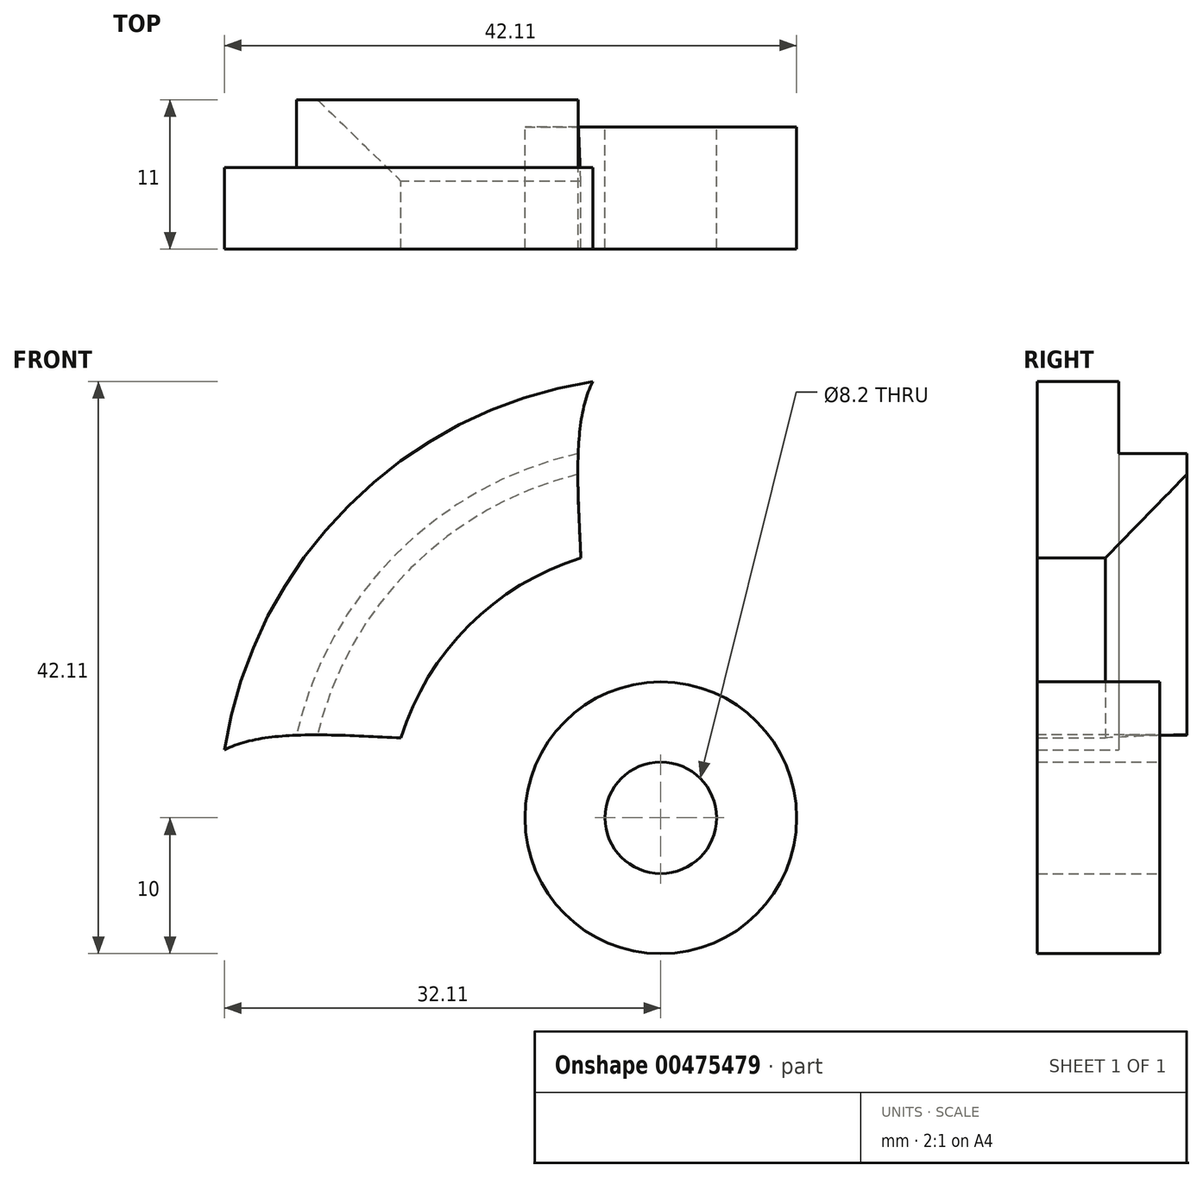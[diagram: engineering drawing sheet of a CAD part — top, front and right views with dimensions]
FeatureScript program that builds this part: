
annotation { "Feature Type Name" : "Feature", "Feature Type Description" : "" }
export const myFeature = defineFeature(function(context is Context, id is Id, definition is map)
    precondition{}
    {
        {
            var Q0;
            Q0=qCreatedBy(makeId("Front.planeOp"),FACE);
            var sketch = newSketch(context, id + "F0", { "sketchPlane" : qUnion([Q0])});
            skArc(sketch, "E0", {"start": v(-22.98, 22.98) * mm, "mid": v(-14.72, -28.98) * mm, "end": v(32.11, -5) * mm});
            skCircle(sketch, "E1", {"center": v(0, 0) * mm, "radius": 27.5 * mm});
            skLineSegment(sketch, "E2", {"start": v(-27.5, 0) * mm, "end": v(27.5, 0) * mm, "construction": true});
            skLineSegment(sketch, "E3", {"start": v(0, 0) * mm, "end": v(22.98, 22.98) * mm, "construction": true});
            skFitSpline(sketch, "E4", {"points": [v(5, 32.11) * mm, v(8, 8) * mm, v(32.11, 5) * mm], "startDerivative": vector(18, -34.81) * mm, "endDerivative": vector(34.81, -18) * mm});
            skArc(sketch, "E5.MirrorC", {"start": v(-5, 32.11) * mm, "mid": v(0, 32.5) * mm, "end": v(5, 32.11) * mm});
            skLineSegment(sketch, "E6.MirrorCS", {"start": v(0, 0) * mm, "end": v(-19.45, 19.45) * mm, "construction": true});
            skFitSpline(sketch, "E7.MirrorCS", {"points": [v(-5, 32.11) * mm, v(-8, 8) * mm, v(-32.11, 5) * mm], "startDerivative": vector(-18, -34.81) * mm, "endDerivative": vector(-34.81, -18) * mm});
            skFitSpline(sketch, "E8.MirrorCS", {"points": [v(-5, 32.11) * mm, v(-8, 8) * mm, v(-32.11, 5) * mm], "startDerivative": vector(-18, -34.81) * mm, "endDerivative": vector(-34.81, -18) * mm});
            skFitSpline(sketch, "E9.MirrorCS", {"points": [v(5, 32.11) * mm, v(8, 8) * mm, v(32.11, 5) * mm], "startDerivative": vector(18, -34.81) * mm, "endDerivative": vector(34.81, -18) * mm});
            skFitSpline(sketch, "E10.MirrorCS", {"points": [v(-5, 32.11) * mm, v(-8, 8) * mm, v(-32.11, 5) * mm], "startDerivative": vector(-18, -34.81) * mm, "endDerivative": vector(-34.81, -18) * mm});
            skFitSpline(sketch, "E11.MirrorCS", {"points": [v(5, 32.11) * mm, v(8, 8) * mm, v(32.11, 5) * mm], "startDerivative": vector(18, -34.81) * mm, "endDerivative": vector(34.81, -18) * mm});
            skLineSegment(sketch, "E12.MirrorCS", {"start": v(0, 0) * mm, "end": v(19.45, 19.45) * mm, "construction": true});
            skFitSpline(sketch, "E13.MirrorCS", {"points": [v(-5, 32.11) * mm, v(-8, 8) * mm, v(-32.11, 5) * mm], "startDerivative": vector(-18, -34.81) * mm, "endDerivative": vector(-34.81, -18) * mm});
            skFitSpline(sketch, "E14.MirrorCS", {"points": [v(5, 32.11) * mm, v(8, 8) * mm, v(32.11, 5) * mm], "startDerivative": vector(18, -34.81) * mm, "endDerivative": vector(34.81, -18) * mm});
            skLineSegment(sketch, "E15.MirrorCS", {"start": v(0, 0) * mm, "end": v(-8, 8) * mm, "construction": true});
            skArc(sketch, "E16.MirrorC", {"start": v(-32.11, 5) * mm, "mid": v(-5, -32.11) * mm, "end": v(32.11, -5) * mm});
            skFitSpline(sketch, "E17.MirrorCS", {"points": [v(-5, 32.11) * mm, v(-8, 8) * mm, v(-32.11, 5) * mm], "startDerivative": vector(-18, -34.81) * mm, "endDerivative": vector(-34.81, -18) * mm});
            skFitSpline(sketch, "E18.MirrorCS", {"points": [v(5, 32.11) * mm, v(8, 8) * mm, v(32.11, 5) * mm], "startDerivative": vector(18, -34.81) * mm, "endDerivative": vector(34.81, -18) * mm});
            skFitSpline(sketch, "E19.MirrorCS", {"points": [v(-5, 32.11) * mm, v(-8, 8) * mm, v(-32.11, 5) * mm], "startDerivative": vector(-18, -34.81) * mm, "endDerivative": vector(-34.81, -18) * mm});
            skArc(sketch, "E20.MirrorC", {"start": v(-6.08, 26.82) * mm, "mid": v(13.29, -24.08) * mm, "end": v(-19.45, 19.45) * mm});
            skFitSpline(sketch, "E21.MirrorCS", {"points": [v(5, 32.11) * mm, v(8, 8) * mm, v(32.11, 5) * mm], "startDerivative": vector(18, -34.81) * mm, "endDerivative": vector(34.81, -18) * mm});
            skCircle(sketch, "E22.MirrorC", {"center": v(0, 0) * mm, "radius": 32.5 * mm});
            skLineSegment(sketch, "E23.MirrorCS", {"start": v(0, 0) * mm, "end": v(-25.12, 25.12) * mm, "construction": true});
            skFitSpline(sketch, "E24.MirrorCS", {"points": [v(-5, 32.11) * mm, v(-8, 8) * mm, v(-32.11, 5) * mm], "startDerivative": vector(-18, -34.81) * mm, "endDerivative": vector(-34.81, -18) * mm});
            skLineSegment(sketch, "E25.MirrorCS", {"start": v(0, 0) * mm, "end": v(25.12, 25.12) * mm, "construction": true});
            skFitSpline(sketch, "E26.MirrorCS", {"points": [v(-5, 32.11) * mm, v(-8, 8) * mm, v(-32.11, 5) * mm], "startDerivative": vector(-18, -34.81) * mm, "endDerivative": vector(-34.81, -18) * mm});
            skFitSpline(sketch, "E27.MirrorCS", {"points": [v(5, 32.11) * mm, v(8, 8) * mm, v(32.11, 5) * mm], "startDerivative": vector(18, -34.81) * mm, "endDerivative": vector(34.81, -18) * mm});
            skLineSegment(sketch, "E28.MirrorCS", {"start": v(27.5, 0) * mm, "end": v(-27.5, 0) * mm, "construction": true});
            skFitSpline(sketch, "E29.MirrorCS", {"points": [v(-5, -32.11) * mm, v(-8, -8) * mm, v(-32.11, -5) * mm], "startDerivative": vector(-18, 34.81) * mm, "endDerivative": vector(-34.81, 18) * mm});
            skFitSpline(sketch, "E30.MirrorCS", {"points": [v(5, -32.11) * mm, v(8, -8) * mm, v(32.11, -5) * mm], "startDerivative": vector(18, 34.81) * mm, "endDerivative": vector(34.81, 18) * mm});
            skFitSpline(sketch, "E31.MirrorCS", {"points": [v(-5, -32.11) * mm, v(-8, -8) * mm, v(-32.11, -5) * mm], "startDerivative": vector(-18, 34.81) * mm, "endDerivative": vector(-34.81, 18) * mm});
            skFitSpline(sketch, "E32.MirrorCS", {"points": [v(5, -32.11) * mm, v(8, -8) * mm, v(32.11, -5) * mm], "startDerivative": vector(18, 34.81) * mm, "endDerivative": vector(34.81, 18) * mm});
            skFitSpline(sketch, "E33.MirrorCS", {"points": [v(-5, -32.11) * mm, v(-8, -8) * mm, v(-32.11, -5) * mm], "startDerivative": vector(-18, 34.81) * mm, "endDerivative": vector(-34.81, 18) * mm});
            skFitSpline(sketch, "E34.MirrorCS", {"points": [v(-5, -32.11) * mm, v(-8, -8) * mm, v(-32.11, -5) * mm], "startDerivative": vector(-18, 34.81) * mm, "endDerivative": vector(-34.81, 18) * mm});
            skFitSpline(sketch, "E35.MirrorCS", {"points": [v(5, -32.11) * mm, v(8, -8) * mm, v(32.11, -5) * mm], "startDerivative": vector(18, 34.81) * mm, "endDerivative": vector(34.81, 18) * mm});
            skFitSpline(sketch, "E36.MirrorCS", {"points": [v(-5, -32.11) * mm, v(-8, -8) * mm, v(-32.11, -5) * mm], "startDerivative": vector(-18, 34.81) * mm, "endDerivative": vector(-34.81, 18) * mm});
            skFitSpline(sketch, "E37.MirrorCS", {"points": [v(5, -32.11) * mm, v(8, -8) * mm, v(32.11, -5) * mm], "startDerivative": vector(18, 34.81) * mm, "endDerivative": vector(34.81, 18) * mm});
            skFitSpline(sketch, "E38.MirrorCS", {"points": [v(-5, -32.11) * mm, v(-8, -8) * mm, v(-32.11, -5) * mm], "startDerivative": vector(-18, 34.81) * mm, "endDerivative": vector(-34.81, 18) * mm});
            skFitSpline(sketch, "E39.MirrorCS", {"points": [v(5, -32.11) * mm, v(8, -8) * mm, v(32.11, -5) * mm], "startDerivative": vector(18, 34.81) * mm, "endDerivative": vector(34.81, 18) * mm});
            skFitSpline(sketch, "E40.MirrorCS", {"points": [v(5, -32.11) * mm, v(8, -8) * mm, v(32.11, -5) * mm], "startDerivative": vector(18, 34.81) * mm, "endDerivative": vector(34.81, 18) * mm});
            skFitSpline(sketch, "E41.MirrorCS", {"points": [v(-5, -32.11) * mm, v(-8, -8) * mm, v(-32.11, -5) * mm], "startDerivative": vector(-18, 34.81) * mm, "endDerivative": vector(-34.81, 18) * mm});
            skFitSpline(sketch, "E42.MirrorCS", {"points": [v(5, -32.11) * mm, v(8, -8) * mm, v(32.11, -5) * mm], "startDerivative": vector(18, 34.81) * mm, "endDerivative": vector(34.81, 18) * mm});
            skFitSpline(sketch, "E43.MirrorCS", {"points": [v(-5, -32.11) * mm, v(-8, -8) * mm, v(-32.11, -5) * mm], "startDerivative": vector(-18, 34.81) * mm, "endDerivative": vector(-34.81, 18) * mm});
            skLineSegment(sketch, "E44.trimOffspring", {"start": v(-22.98, 22.98) * mm, "end": v(-25.12, 25.12) * mm, "construction": true});
            skLineSegment(sketch, "E45.trimOffspring", {"start": v(-19.45, 19.45) * mm, "end": v(-25.12, 25.12) * mm, "construction": true});
            skArc(sketch, "E46.trimOffspring", {"start": v(5, 32.11) * mm, "mid": v(0, 32.5) * mm, "end": v(-5, 32.11) * mm});
            skArc(sketch, "E47.trimOffspring", {"start": v(32.11, 5) * mm, "mid": v(-10.08, -30.9) * mm, "end": v(-22.98, 22.98) * mm});
            skArc(sketch, "E48.trimOffspring", {"start": v(22.98, 22.98) * mm, "mid": v(10.08, 30.9) * mm, "end": v(-5, 32.11) * mm});
            skLineSegment(sketch, "E49.trimOffspring", {"start": v(22.98, 22.98) * mm, "end": v(25.12, 25.12) * mm, "construction": true});
            skCircle(sketch, "E50", {"center": v(0, 0) * mm, "radius": 4.1 * mm});
            skCircle(sketch, "E51", {"center": v(0, 0) * mm, "radius": 10 * mm});
            skCircle(sketch, "E52", {"center": v(0, 0) * mm, "radius": 20 * mm});
            skSolve(sketch);
        }
        {
            var Q0;
            {var subQ0=sQuery(id+"F0.wireOp",EDGE,"E27.MirrorCS");var subQ1=sQuery(id+"F0.wireOp",EDGE,"E1");var subQ11=makeQuery(id+"F0.imprint","INTERSECT",VERTEX,{"disambiguationData":[OD(0.0)],"derivedFrom":[subQ1,subQ0]});Q0=makeQuery(id+"F0.imprint","IMPRINT",FACE,{"disambiguationData":[TD([[makeQuery(id+"F0.imprint","IMPRINT",EDGE,{"disambiguationData":[TD([[subQ11,-1.0]])],"derivedFrom":subQ1}),1.0]])]});}
            var Q1;
            {var subQ0=sQuery(id+"F0.wireOp",EDGE,"E27.MirrorCS");var subQ1=sQuery(id+"F0.wireOp",EDGE,"E1");var subQ2=makeQuery(id+"F0.imprint","INTERSECT",VERTEX,{"disambiguationData":[OD(1.0)],"derivedFrom":[subQ1,subQ0]});Q1=makeQuery(id+"F0.imprint","IMPRINT",FACE,{"disambiguationData":[TD([[makeQuery(id+"F0.imprint","IMPRINT",EDGE,{"disambiguationData":[TD([[subQ2,1.0]])],"derivedFrom":subQ1}),-1.0]])]});}
            var Q2;
            {var subQ0=sQuery(id+"F0.wireOp",EDGE,"E27.MirrorCS");var subQ1=sQuery(id+"F0.wireOp",EDGE,"E1");var subQ2=makeQuery(id+"F0.imprint","INTERSECT",VERTEX,{"disambiguationData":[OD(0.0)],"derivedFrom":[subQ1,subQ0]});Q2=makeQuery(id+"F0.imprint","IMPRINT",FACE,{"disambiguationData":[TD([[makeQuery(id+"F0.imprint","IMPRINT",EDGE,{"disambiguationData":[TD([[subQ2,-1.0]])],"derivedFrom":subQ1}),-1.0]])]});}
            var Q3;
            {var subQ0=sQuery(id+"F0.wireOp",EDGE,"E43.MirrorCS");var subQ1=sQuery(id+"F0.wireOp",EDGE,"E1");var subQ2=makeQuery(id+"F0.imprint","INTERSECT",VERTEX,{"disambiguationData":[OD(1.0)],"derivedFrom":[subQ1,subQ0]});Q3=makeQuery(id+"F0.imprint","IMPRINT",FACE,{"disambiguationData":[TD([[makeQuery(id+"F0.imprint","IMPRINT",EDGE,{"disambiguationData":[TD([[subQ2,-1.0]])],"derivedFrom":subQ1}),-1.0]])]});}
            var Q4;
            {var subQ0=sQuery(id+"F0.wireOp",EDGE,"E26.MirrorCS");var subQ1=sQuery(id+"F0.wireOp",EDGE,"E1");var subQ2=makeQuery(id+"F0.imprint","INTERSECT",VERTEX,{"disambiguationData":[OD(1.0)],"derivedFrom":[subQ1,subQ0]});Q4=makeQuery(id+"F0.imprint","IMPRINT",FACE,{"disambiguationData":[TD([[makeQuery(id+"F0.imprint","IMPRINT",EDGE,{"disambiguationData":[TD([[subQ2,-1.0]])],"derivedFrom":subQ1}),-1.0]])]});}
            var Q5;
            Q5=makeQuery(id+"F0.imprint","IMPRINT",FACE,{"disambiguationData":[TD([[makeQuery(id+"F0.imprint","IMPRINT",EDGE,{"derivedFrom":sQuery(id+"F0.wireOp",EDGE,"E51")}),-1.0]])]});
            var Q6;
            {var subQ0=sQuery(id+"F0.wireOp",EDGE,"E43.MirrorCS");var subQ1=sQuery(id+"F0.wireOp",EDGE,"E1");var subQ2=makeQuery(id+"F0.imprint","INTERSECT",VERTEX,{"disambiguationData":[OD(1.0)],"derivedFrom":[subQ1,subQ0]});Q6=makeQuery(id+"F0.imprint","IMPRINT",FACE,{"disambiguationData":[TD([[makeQuery(id+"F0.imprint","IMPRINT",EDGE,{"disambiguationData":[TD([[subQ2,-1.0]])],"derivedFrom":subQ1}),1.0]])]});}
            var Q7;
            {var subQ0=sQuery(id+"F0.wireOp",EDGE,"E27.MirrorCS");var subQ1=sQuery(id+"F0.wireOp",EDGE,"E1");var subQ2=makeQuery(id+"F0.imprint","INTERSECT",VERTEX,{"disambiguationData":[OD(1.0)],"derivedFrom":[subQ1,subQ0]});Q7=makeQuery(id+"F0.imprint","IMPRINT",FACE,{"disambiguationData":[TD([[makeQuery(id+"F0.imprint","IMPRINT",EDGE,{"disambiguationData":[TD([[subQ2,1.0]])],"derivedFrom":subQ1}),1.0]])]});}
            var Q8;
            {var subQ0=sQuery(id+"F0.wireOp",EDGE,"E26.MirrorCS");var subQ1=sQuery(id+"F0.wireOp",EDGE,"E1");var subQ2=makeQuery(id+"F0.imprint","INTERSECT",VERTEX,{"disambiguationData":[OD(1.0)],"derivedFrom":[subQ1,subQ0]});Q8=makeQuery(id+"F0.imprint","IMPRINT",FACE,{"disambiguationData":[TD([[makeQuery(id+"F0.imprint","IMPRINT",EDGE,{"disambiguationData":[TD([[subQ2,-1.0]])],"derivedFrom":subQ1}),1.0]])]});}
            var Q9;
            Q9=makeQuery(id+"F0.imprint","IMPRINT",FACE,{"disambiguationData":[TD([[makeQuery(id+"F0.imprint","IMPRINT",EDGE,{"derivedFrom":sQuery(id+"F0.wireOp",EDGE,"E50")}),-1.0]])]});
            extrude(context, id + "F1", {"entities" : qUnion([Q0, Q1, Q2, Q3, Q4, Q5, Q6, Q7, Q8, Q9]), "depth" : 6 * mm, "offsetDistance" : 25 * mm});
        }
        {
            var Q0;
            {var subQ0=sQuery(id+"F0.wireOp",EDGE,"E27.MirrorCS");var subQ1=sQuery(id+"F0.wireOp",EDGE,"E1");var subQ2=makeQuery(id+"F0.imprint","INTERSECT",VERTEX,{"disambiguationData":[OD(0.0)],"derivedFrom":[subQ1,subQ0]});Q0=makeQuery(id+"F0.imprint","IMPRINT",FACE,{"disambiguationData":[TD([[makeQuery(id+"F0.imprint","IMPRINT",EDGE,{"disambiguationData":[TD([[subQ2,-1.0]])],"derivedFrom":subQ1}),1.0]])]});}
            var Q1;
            {var subQ0=sQuery(id+"F0.wireOp",EDGE,"E27.MirrorCS");var subQ1=sQuery(id+"F0.wireOp",EDGE,"E1");var subQ2=makeQuery(id+"F0.imprint","INTERSECT",VERTEX,{"disambiguationData":[OD(1.0)],"derivedFrom":[subQ1,subQ0]});Q1=makeQuery(id+"F0.imprint","IMPRINT",FACE,{"disambiguationData":[TD([[makeQuery(id+"F0.imprint","IMPRINT",EDGE,{"disambiguationData":[TD([[subQ2,1.0]])],"derivedFrom":subQ1}),1.0]])]});}
            var Q2;
            {var subQ0=sQuery(id+"F0.wireOp",EDGE,"E26.MirrorCS");var subQ1=sQuery(id+"F0.wireOp",EDGE,"E1");var subQ2=makeQuery(id+"F0.imprint","INTERSECT",VERTEX,{"disambiguationData":[OD(1.0)],"derivedFrom":[subQ1,subQ0]});Q2=makeQuery(id+"F0.imprint","IMPRINT",FACE,{"disambiguationData":[TD([[makeQuery(id+"F0.imprint","IMPRINT",EDGE,{"disambiguationData":[TD([[subQ2,-1.0]])],"derivedFrom":subQ1}),1.0]])]});}
            var Q3;
            {var subQ0=sQuery(id+"F0.wireOp",EDGE,"E43.MirrorCS");var subQ1=sQuery(id+"F0.wireOp",EDGE,"E1");var subQ2=makeQuery(id+"F0.imprint","INTERSECT",VERTEX,{"disambiguationData":[OD(1.0)],"derivedFrom":[subQ1,subQ0]});Q3=makeQuery(id+"F0.imprint","IMPRINT",FACE,{"disambiguationData":[TD([[makeQuery(id+"F0.imprint","IMPRINT",EDGE,{"disambiguationData":[TD([[subQ2,-1.0]])],"derivedFrom":subQ1}),1.0]])]});}
            extrude(context, id + "F2", {"entities" : qUnion([Q0, Q1, Q2, Q3]), "operationType" : NewBodyOperationType.ADD, "oppositeDirection" : true, "depth" : 5 * mm, "offsetDistance" : 25 * mm});
        }
        {
            var Q0;
            {var subQ0=sQuery(id+"F0.wireOp",EDGE,"E52");Q0=makeQuery(id+"F2.opExtrude","CAP_EDGE",EDGE,{"disambiguationData":[OSD([subQ0]),TDD([makeQuery(id+"F0.imprint","IMPRINT",EDGE,{"disambiguationData":[TD([[makeQuery(id+"F0.imprint","INTERSECT",VERTEX,{"disambiguationData":[OD(0.0)],"derivedFrom":[sQuery(id+"F0.wireOp",EDGE,"E26.MirrorCS"),subQ0]}),1.0]])],"derivedFrom":subQ0})])],"isStart":false});}
            var Q1;
            {var subQ0=sQuery(id+"F0.wireOp",EDGE,"E52");Q1=makeQuery(id+"F2.opExtrude","CAP_EDGE",EDGE,{"disambiguationData":[OSD([subQ0]),TDD([makeQuery(id+"F0.imprint","IMPRINT",EDGE,{"disambiguationData":[TD([[makeQuery(id+"F0.imprint","INTERSECT",VERTEX,{"disambiguationData":[OD(1.0)],"derivedFrom":[sQuery(id+"F0.wireOp",EDGE,"E27.MirrorCS"),subQ0]}),1.0]])],"derivedFrom":subQ0})])],"isStart":false});}
            var Q2;
            {var subQ0=sQuery(id+"F0.wireOp",EDGE,"E52");Q2=makeQuery(id+"F2.opExtrude","CAP_EDGE",EDGE,{"disambiguationData":[OSD([subQ0]),TDD([makeQuery(id+"F0.imprint","IMPRINT",EDGE,{"disambiguationData":[TD([[makeQuery(id+"F0.imprint","INTERSECT",VERTEX,{"disambiguationData":[OD(1.0)],"derivedFrom":[sQuery(id+"F0.wireOp",EDGE,"E26.MirrorCS"),subQ0]}),-1.0]])],"derivedFrom":subQ0})])],"isStart":false});}
            var Q3;
            {var subQ0=sQuery(id+"F0.wireOp",EDGE,"E52");Q3=makeQuery(id+"F2.opExtrude","CAP_EDGE",EDGE,{"disambiguationData":[OSD([subQ0]),TDD([makeQuery(id+"F0.imprint","IMPRINT",EDGE,{"disambiguationData":[TD([[makeQuery(id+"F0.imprint","INTERSECT",VERTEX,{"disambiguationData":[OD(0.0)],"derivedFrom":[sQuery(id+"F0.wireOp",EDGE,"E42.MirrorCS"),subQ0]}),1.0]])],"derivedFrom":subQ0})])],"isStart":false});}
            chamfer(context, id + "F3", {"entities" : qUnion([Q0, Q1, Q2, Q3]), "width" : 6 * mm, "tangentPropagation" : true});
        }
        {
            var Q0;
            Q0=makeQuery(id+"F0.imprint","IMPRINT",FACE,{"disambiguationData":[TD([[makeQuery(id+"F0.imprint","IMPRINT",EDGE,{"derivedFrom":sQuery(id+"F0.wireOp",EDGE,"E50")}),-1.0]])]});
            extrude(context, id + "F4", {"entities" : qUnion([Q0]), "operationType" : NewBodyOperationType.ADD, "oppositeDirection" : true, "depth" : 3 * mm, "offsetDistance" : 25 * mm});
        }
    });
